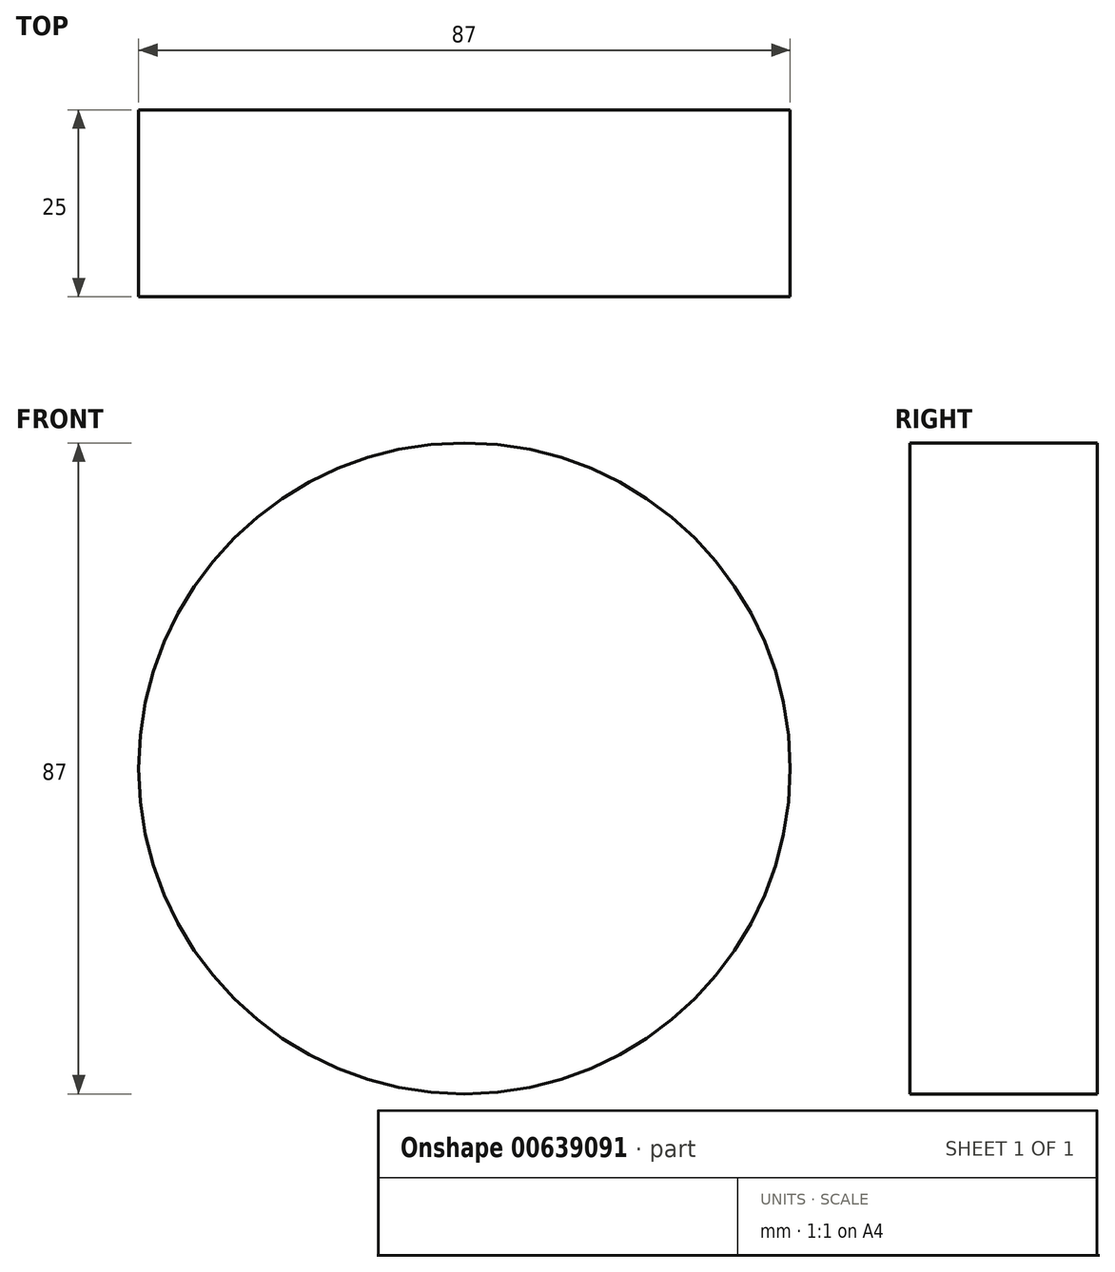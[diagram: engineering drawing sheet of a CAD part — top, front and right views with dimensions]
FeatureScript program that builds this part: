
annotation { "Feature Type Name" : "Feature", "Feature Type Description" : "" }
export const myFeature = defineFeature(function(context is Context, id is Id, definition is map)
    precondition{}
    {
        {
            var Q0;
            Q0=qCreatedBy(makeId("Front.planeOp"),FACE);
            var sketch = newSketch(context, id + "F0", { "sketchPlane" : qUnion([Q0])});
            skCircle(sketch, "E0", {"center": v(0, 0) * mm, "radius": 43.5 * mm});
            skSolve(sketch);
        }
        {
            var Q0;
            Q0 = qSketchRegion(id + "F0", true);
            extrude(context, id + "F1", {"entities" : qUnion([Q0]), "depth" : 25 * mm, "offsetDistance" : 25 * mm});
        }
    });
